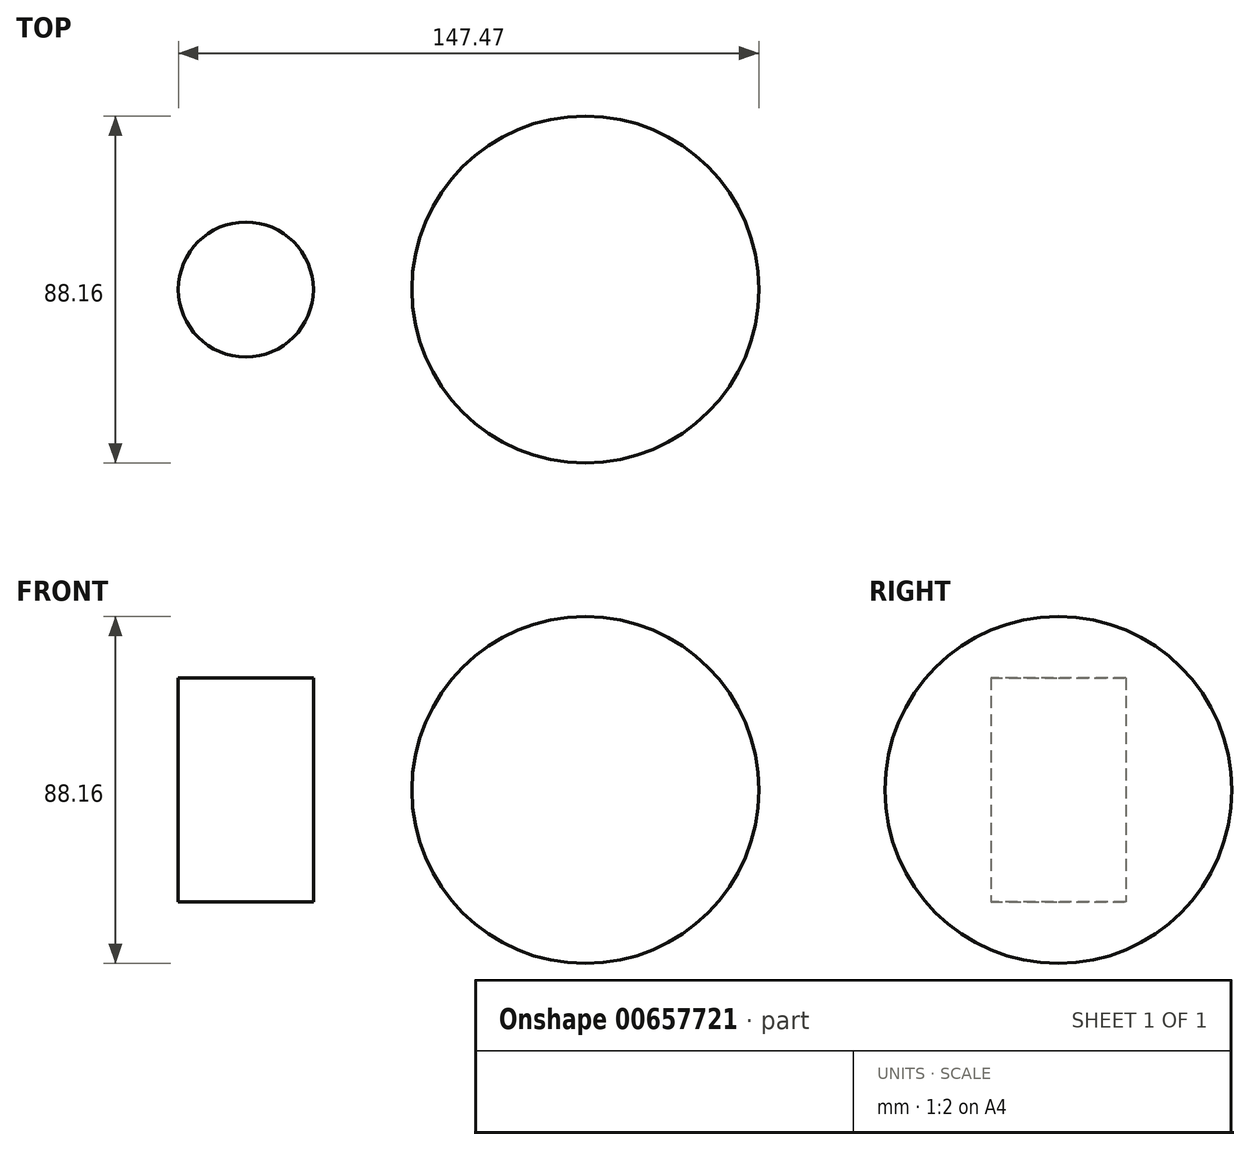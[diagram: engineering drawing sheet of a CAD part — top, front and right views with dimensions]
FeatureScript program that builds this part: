
annotation { "Feature Type Name" : "Feature", "Feature Type Description" : "" }
export const myFeature = defineFeature(function(context is Context, id is Id, definition is map)
    precondition{}
    {
        {
            var Q0;
            Q0=qCreatedBy(makeId("Top.planeOp"),FACE);
            var sketch = newSketch(context, id + "F0", { "sketchPlane" : qUnion([Q0])});
            skCircle(sketch, "E0", {"center": v(-69.06, 0) * mm, "radius": 17.15 * mm});
            skLineSegment(sketch, "E1", {"start": v(-26.88, 0) * mm, "end": v(61.27, 0) * mm});
            skArc(sketch, "E2", {"start": v(-26.88, 0) * mm, "mid": v(17.2, 44.08) * mm, "end": v(61.27, 0) * mm});
            skSolve(sketch);
        }
        {
            var Q0;
            Q0=makeQuery(id+"F0.imprint","IMPRINT",FACE,{"disambiguationData":[TD([[makeQuery(id+"F0.imprint","IMPRINT",EDGE,{"derivedFrom":sQuery(id+"F0.wireOp",EDGE,"E1")}),1.0]])]});
            var Q1;
            Q1=sQuery(id+"F0.wireOp",EDGE,"E1");
            revolve(context, id + "F1", {"entities" : qUnion([Q0]), "axis" : qUnion([Q1]), "revolveType" : RevolveType.FULL});
        }
        {
            var Q0;
            Q0=makeQuery(id+"F0.imprint","IMPRINT",FACE,{"disambiguationData":[TD([[makeQuery(id+"F0.imprint","IMPRINT",EDGE,{"derivedFrom":sQuery(id+"F0.wireOp",EDGE,"E0")}),1.0]])]});
            extrude(context, id + "F2", {"entities" : qUnion([Q0]), "endBound" : BoundingType.SYMMETRIC, "depth" : 56.9 * mm, "offsetDistance" : 25.4 * mm});
        }
    });
